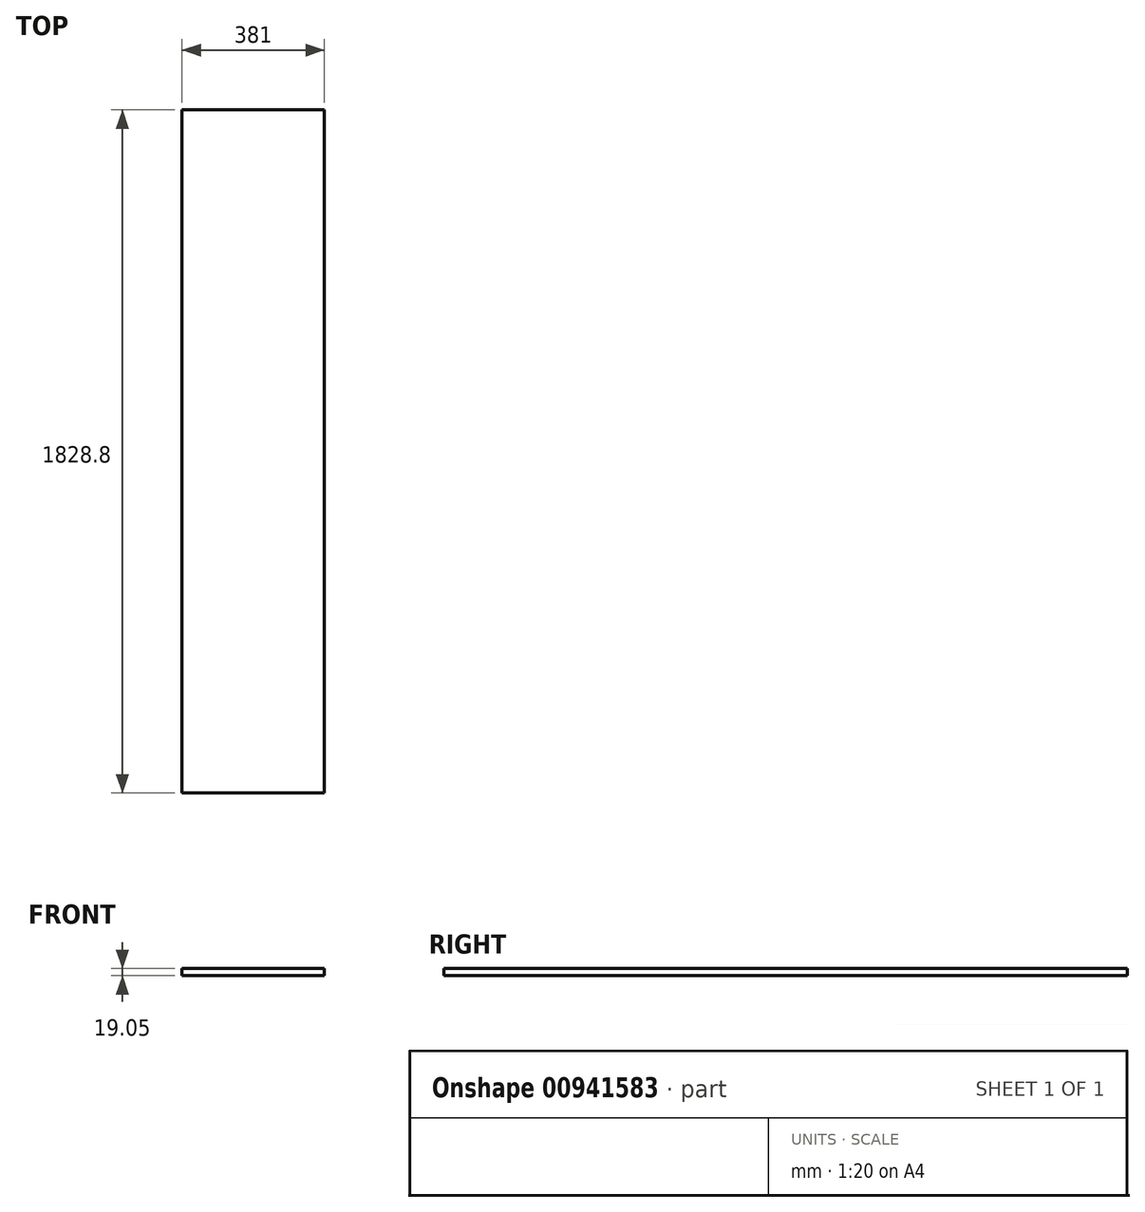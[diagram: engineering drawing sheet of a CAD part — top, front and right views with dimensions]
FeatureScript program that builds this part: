
annotation { "Feature Type Name" : "Feature", "Feature Type Description" : "" }
export const myFeature = defineFeature(function(context is Context, id is Id, definition is map)
    precondition{}
    {
        {
            var Q0;
            Q0=qCreatedBy(makeId("Front.planeOp"),FACE);
            var sketch = newSketch(context, id + "F0", { "sketchPlane" : qUnion([Q0])});
            skLineSegment(sketch, "E0.bottom", {"start": v(-305.46, -33.65) * mm, "end": v(75.54, -33.65) * mm});
            skLineSegment(sketch, "E0.top", {"start": v(-305.46, -52.7) * mm, "end": v(75.54, -52.7) * mm});
            skLineSegment(sketch, "E0.left", {"start": v(-305.46, -33.65) * mm, "end": v(-305.46, -52.7) * mm});
            skLineSegment(sketch, "E0.right", {"start": v(75.54, -33.65) * mm, "end": v(75.54, -52.7) * mm});
            skSolve(sketch);
        }
        {
            var Q0;
            Q0 = qSketchRegion(id + "F0", true);
            extrude(context, id + "F1", {"entities" : qUnion([Q0]), "depth" : 1828.8 * mm, "offsetDistance" : 25.4 * mm});
        }
    });
